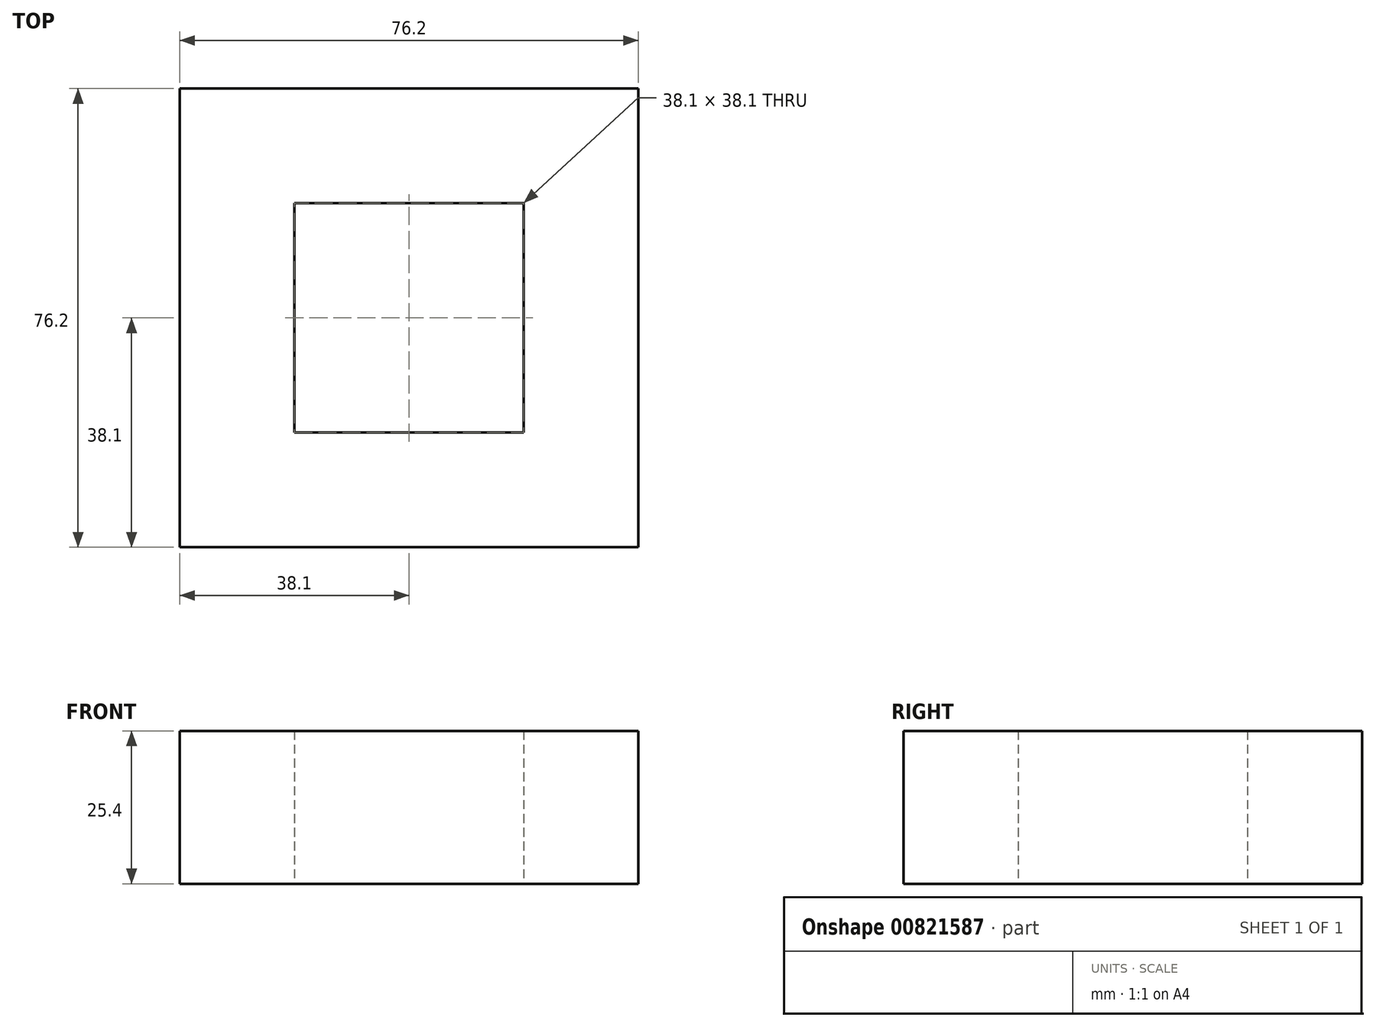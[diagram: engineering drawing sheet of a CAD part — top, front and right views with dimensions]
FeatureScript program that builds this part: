
annotation { "Feature Type Name" : "Feature", "Feature Type Description" : "" }
export const myFeature = defineFeature(function(context is Context, id is Id, definition is map)
    precondition{}
    {
        {
            var Q0;
            Q0=qCreatedBy(makeId("Top.planeOp"),FACE);
            var sketch = newSketch(context, id + "F0", { "sketchPlane" : qUnion([Q0])});
            skLineSegment(sketch, "E0.bottom", {"start": v(38.1, 38.1) * mm, "end": v(-38.1, 38.1) * mm});
            skLineSegment(sketch, "E0.top", {"start": v(38.1, -38.1) * mm, "end": v(-38.1, -38.1) * mm});
            skLineSegment(sketch, "E0.left", {"start": v(38.1, 38.1) * mm, "end": v(38.1, -38.1) * mm});
            skLineSegment(sketch, "E0.right", {"start": v(-38.1, 38.1) * mm, "end": v(-38.1, -38.1) * mm});
            skPoint(sketch, "E0.middle", {"position": v(0, 0) * mm});
            skLineSegment(sketch, "E1.bottom", {"start": v(19.05, 19.05) * mm, "end": v(-19.05, 19.05) * mm});
            skLineSegment(sketch, "E1.top", {"start": v(19.05, -19.05) * mm, "end": v(-19.05, -19.05) * mm});
            skLineSegment(sketch, "E1.left", {"start": v(19.05, 19.05) * mm, "end": v(19.05, -19.05) * mm});
            skLineSegment(sketch, "E1.right", {"start": v(-19.05, 19.05) * mm, "end": v(-19.05, -19.05) * mm});
            skSolve(sketch);
        }
        {
            var Q0;
            Q0=makeQuery(id+"F0.imprint","IMPRINT",FACE,{"disambiguationData":[TD([[makeQuery(id+"F0.imprint","IMPRINT",EDGE,{"derivedFrom":sQuery(id+"F0.wireOp",EDGE,"E0.bottom")}),1.0]])]});
            extrude(context, id + "F1", {"entities" : qUnion([Q0]), "depth" : 25.4 * mm, "offsetDistance" : 25.4 * mm});
        }
    });
